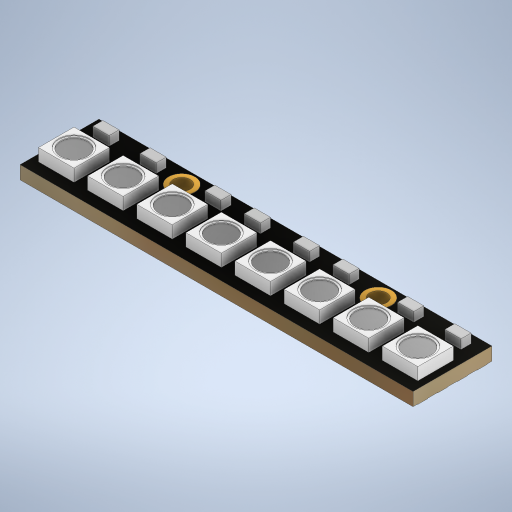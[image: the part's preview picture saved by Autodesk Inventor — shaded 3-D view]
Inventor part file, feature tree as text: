
AUTODESK INVENTOR PART (.ipt)
format: ipt  version: 2023 (Build 270158000, 158)  size: 532,480 bytes
history: native  units: mm
features: extrude x7, sketch x7, plane x2, hole x1, mirror x1
ambient origin geometry x8: Origin, YZ Plane, XZ Plane, XY Plane, X Axis, Y Axis, Z Axis, Center Point
bodies: Solid1 (feature_tree)
feature tree (18):
  extrude  "Extrusion1"  Depth=10.2mm
  extrude  "Extrusion2"  Depth=4.6mm
  sketch  "Sketch3"  dims[d5=4.6mm d6=0.875mm]
  extrude  "Extrusion3"  Depth=0.875mm
  extrude  "Extrusion4"  Depth=6.35mm
  hole  "Hole1"  [1 undecoded]
  extrude  "Extrusion5"  Depth=6.35mm
  plane  "Work Plane1"
  extrude  "Extrusion6"  Depth=0.1mm TaperAngle=0.0deg
  extrude  "Extrusion7"  Depth=12.7mm
  mirror  "Mirror1"
  plane  "Work Plane2"
  sketch  "Sketch1"  dims[d0=50.8mm d1=10.2mm]
  sketch  "Sketch2"  dims[d2=1.7mm d3=0.0mm d4=4.6mm]
  sketch  "Sketch4"  dims[d7=1.5mm d8=80.0mm d10=6.35mm d11=10.0mm d13=10.0mm]
  sketch  "Sketch5"  dims[d15=3.3mm d16=0.0mm d17=4.0mm]
  sketch  "Sketch6"  dims[d18=3.5mm d19=80.0mm d21=6.35mm d22=10.0mm d24=10.0mm]
  sketch  "Sketch7"  dims[d26=0.2mm d27=0.0mm d28=0.1mm d29=0.0mm d30=2.2mm d31=6.0mm d32=4.0mm d33=2.0mm d34=90.0deg d35=8.0mm d36=0.0mm d37=12.7mm d39=12.7mm d40=2.0mm d41=2.1mm d42=1.3mm d43=3.7mm d44=2.4mm d45=2.1mm d46=1.3mm d47=2.1mm d48=1.3mm d49=2.1mm d50=1.3mm d51=4.0mm d52=1.2mm d53=0.0mm d54=2.5mm d55=1.3mm d56=40.0mm d58=2.55mm d59=10.0mm d61=10.0mm d63=0.625mm d64=3.4mm d65=0.05mm d66=0.0mm d67=3.4mm d68=0.05mm d69=0.0mm]
note: 1 required parameter value undecoded (feature->parameter linkage not recoverable at this tier; creation-order binding heuristic only, values carry confidence <= 0.55)
